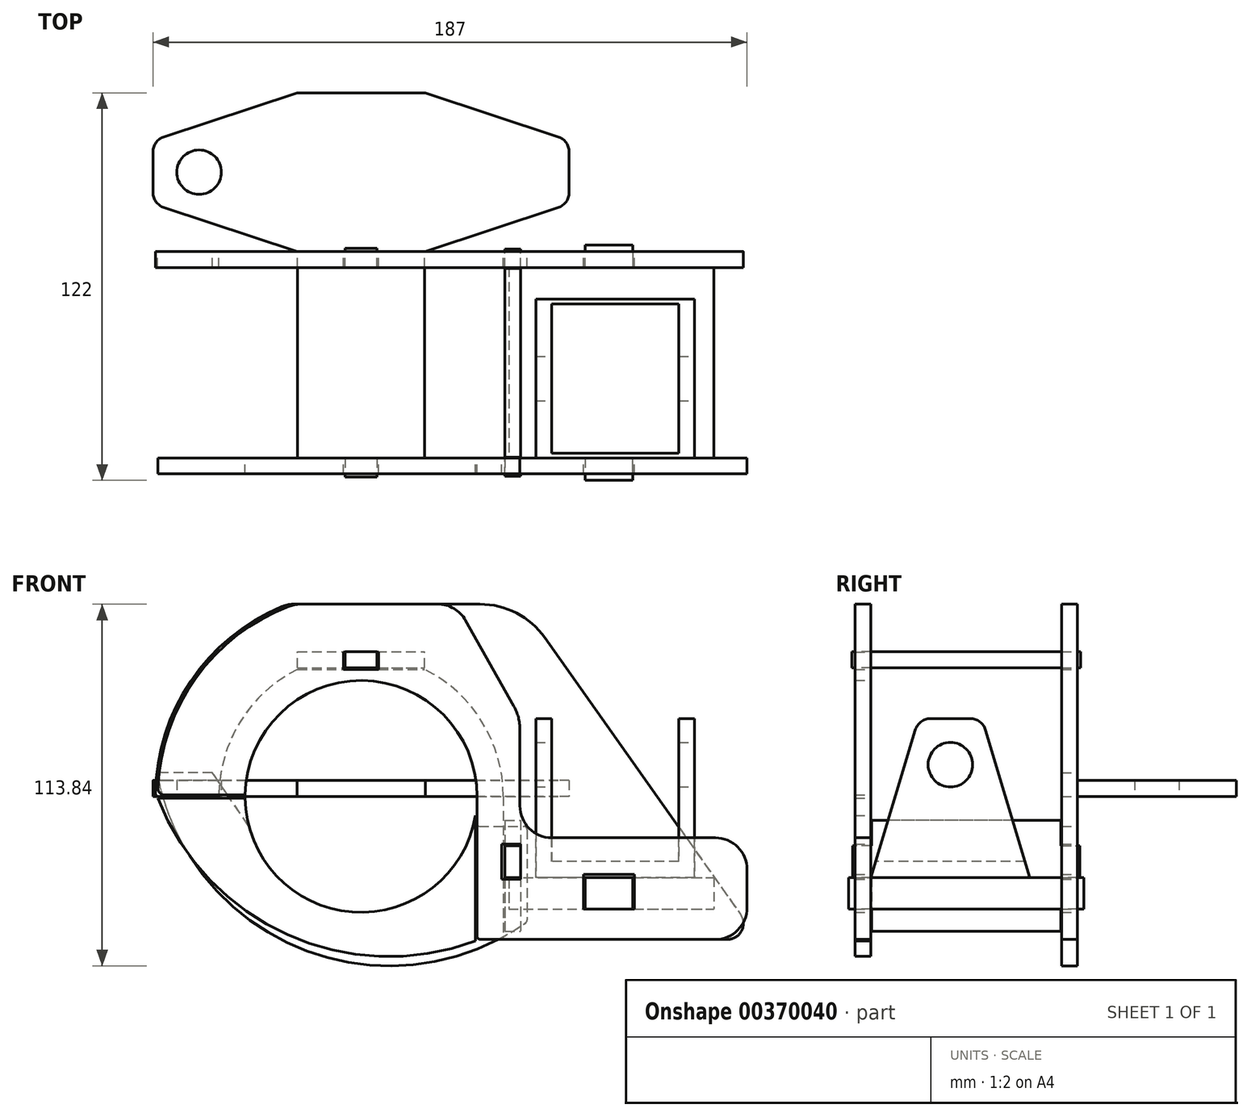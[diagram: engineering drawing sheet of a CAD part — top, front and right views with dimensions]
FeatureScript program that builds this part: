
annotation { "Feature Type Name" : "Feature", "Feature Type Description" : "" }
export const myFeature = defineFeature(function(context is Context, id is Id, definition is map)
    precondition{}
    {
        {
            var Q0;
            Q0=qCreatedBy(makeId("Front.planeOp"),FACE);
            var sketch = newSketch(context, id + "F0", { "sketchPlane" : qUnion([Q0])});
            skArc(sketch, "E0", {"start": v(44.75, 0) * mm, "mid": v(0, 44.75) * mm, "end": v(-44.75, 0) * mm, "construction": true});
            skLineSegment(sketch, "E1", {"start": v(-20, 40.03) * mm, "end": v(-5.5, 40.03) * mm});
            skLineSegment(sketch, "E2", {"start": v(-5.5, 40.03) * mm, "end": v(-5.5, 45.53) * mm});
            skLineSegment(sketch, "E3", {"start": v(-5.5, 45.53) * mm, "end": v(5.5, 45.53) * mm});
            skLineSegment(sketch, "E4", {"start": v(5.5, 45.53) * mm, "end": v(5.5, 40.03) * mm});
            skLineSegment(sketch, "E5", {"start": v(5.5, 40.03) * mm, "end": v(20, 40.03) * mm});
            skPoint(sketch, "E6", {"position": v(0, 45.53) * mm});
            skArc(sketch, "E7", {"start": v(-20, 40.03) * mm, "mid": v(-38.06, 23.53) * mm, "end": v(-44.75, 0) * mm});
            skArc(sketch, "E8", {"start": v(44.75, 0) * mm, "mid": v(38.06, 23.53) * mm, "end": v(20, 40.03) * mm});
            skArc(sketch, "E9.0", {"start": v(-24.92, 59.76) * mm, "mid": v(-53.6, 36.33) * mm, "end": v(-64.74, 1.02) * mm});
            skLineSegment(sketch, "E10", {"start": v(-63.74, 0) * mm, "end": v(-44.75, 0) * mm});
            skLineSegment(sketch, "E11", {"start": v(-21.07, 60.53) * mm, "end": v(37.4, 60.53) * mm});
            skLineSegment(sketch, "E12", {"start": v(44.75, 0) * mm, "end": v(44.75, -15) * mm});
            skLineSegment(sketch, "E13", {"start": v(44.75, -45) * mm, "end": v(115.34, -45) * mm});
            skArc(sketch, "E14", {"start": v(-36.5, 0) * mm, "mid": v(0, -36.5) * mm, "end": v(36.5, 0) * mm, "construction": true});
            skLineSegment(sketch, "E15", {"start": v(-44.75, 0) * mm, "end": v(-36.5, 0) * mm, "construction": true});
            skLineSegment(sketch, "E16", {"start": v(44.75, 0) * mm, "end": v(36.5, 0) * mm, "construction": true});
            skPoint(sketch, "E17", {"position": v(80, 10) * mm});
            skLineSegment(sketch, "E18", {"start": v(57.82, 49.97) * mm, "end": v(119.42, -37.11) * mm});
            skLineSegment(sketch, "E19.bottom", {"start": v(70, -24.5) * mm, "end": v(86, -24.5) * mm});
            skLineSegment(sketch, "E19.top", {"start": v(70, -35.5) * mm, "end": v(86, -35.5) * mm});
            skLineSegment(sketch, "E19.left", {"start": v(70, -24.5) * mm, "end": v(70, -35.5) * mm});
            skLineSegment(sketch, "E19.right", {"start": v(86, -24.5) * mm, "end": v(86, -35.5) * mm});
            skPoint(sketch, "E20.visualSharp", {"position": v(-22.99, 60.53) * mm});
            skArc(sketch, "E20.filletArc", {"start": v(-21.07, 60.53) * mm, "mid": v(-23.04, 60.34) * mm, "end": v(-24.92, 59.76) * mm});
            skPoint(sketch, "E21.visualSharp", {"position": v(50.35, 60.53) * mm});
            skArc(sketch, "E21.filletArc", {"start": v(57.82, 49.97) * mm, "mid": v(48.9, 57.73) * mm, "end": v(37.4, 60.53) * mm});
            skPoint(sketch, "E22.visualSharp", {"position": v(125, -45) * mm});
            skArc(sketch, "E22.filletArc", {"start": v(115.34, -45) * mm, "mid": v(119.78, -42.3) * mm, "end": v(119.42, -37.11) * mm});
            skLineSegment(sketch, "E23", {"start": v(44.75, -15) * mm, "end": v(50.25, -15) * mm});
            skLineSegment(sketch, "E24", {"start": v(50.25, -15) * mm, "end": v(50.25, -26) * mm});
            skLineSegment(sketch, "E25", {"start": v(50.25, -26) * mm, "end": v(44.75, -26) * mm});
            skLineSegment(sketch, "E26.trimOffspring", {"start": v(44.75, -26) * mm, "end": v(44.75, -45) * mm});
            skPoint(sketch, "E27.visualSharp", {"position": v(-64.75, 0) * mm});
            skArc(sketch, "E27.filletArc", {"start": v(-64.74, 1.02) * mm, "mid": v(-64.45, 0.3) * mm, "end": v(-63.74, 0) * mm});
            skSolve(sketch);
        }
        {
            var Q0;
            Q0=qSketchRegion(id+"F0",true);
            var Q1;
            Q1=qConstructionFilter(qBodyType(qCreatedBy(id+"F0",EDGE),BodyType.WIRE),ConstructionObject.NO);
            extrude(context, id + "F1", {"entities" : qUnion([Q0]), "surfaceEntities" : qUnion([Q1]), "depth" : 5 * mm});
        }
        {
            var Q0;
            Q0=qCreatedBy(makeId("Front.planeOp"),FACE);
            var sketch = newSketch(context, id + "F2", { "sketchPlane" : qUnion([Q0])});
            skArc(sketch, "E28", {"start": v(-35.15, -9.84) * mm, "mid": v(-0.7, -36.5) * mm, "end": v(34.75, -11.18) * mm});
            skLineSegment(sketch, "E29", {"start": v(-35.26, -9.45) * mm, "end": v(0, 0) * mm, "construction": true});
            skLineSegment(sketch, "E30", {"start": v(35.26, -9.45) * mm, "end": v(0, 0) * mm, "construction": true});
            skLineSegment(sketch, "E31", {"start": v(-35.5, -9.1) * mm, "end": v(-46.81, 7.5) * mm});
            skLineSegment(sketch, "E32", {"start": v(-46.81, 7.5) * mm, "end": v(-63.1, 7.5) * mm});
            skLineSegment(sketch, "E33", {"start": v(37.13, -9.45) * mm, "end": v(51.25, -9.45) * mm});
            skLineSegment(sketch, "E34", {"start": v(52.25, -10.45) * mm, "end": v(52.25, -38.93) * mm});
            skArc(sketch, "E35", {"start": v(-64.08, 6.3) * mm, "mid": v(-18.57, -48.04) * mm, "end": v(51.83, -39.75) * mm});
            skPoint(sketch, "E36.visualSharp", {"position": v(-35.26, -9.45) * mm});
            skArc(sketch, "E36.filletArc", {"start": v(-35.15, -9.84) * mm, "mid": v(-35.3, -9.46) * mm, "end": v(-35.5, -9.1) * mm});
            skPoint(sketch, "E37.visualSharp", {"position": v(35.26, -9.45) * mm});
            skArc(sketch, "E37.filletArc", {"start": v(37.13, -9.45) * mm, "mid": v(35.65, -9.93) * mm, "end": v(34.75, -11.18) * mm});
            skPoint(sketch, "E38.visualSharp", {"position": v(-64.31, 7.5) * mm});
            skArc(sketch, "E38.filletArc", {"start": v(-63.1, 7.5) * mm, "mid": v(-63.87, 7.13) * mm, "end": v(-64.08, 6.3) * mm});
            skPoint(sketch, "E39.visualSharp", {"position": v(52.25, -39.45) * mm});
            skArc(sketch, "E39.filletArc", {"start": v(51.83, -39.75) * mm, "mid": v(52.14, -39.4) * mm, "end": v(52.25, -38.93) * mm});
            skPoint(sketch, "E40.visualSharp", {"position": v(52.25, -9.45) * mm});
            skArc(sketch, "E40.filletArc", {"start": v(52.25, -10.45) * mm, "mid": v(51.96, -9.74) * mm, "end": v(51.25, -9.45) * mm});
            skSolve(sketch);
        }
        {
            var Q0;
            Q0=qSketchRegion(id+"F2",true);
            extrude(context, id + "F3", {"entities" : qUnion([Q0]), "depth" : 5 * mm});
        }
        {
            var Q0;
            Q0=makeQuery(id+"F1.opExtrude","SWEPT_FACE",FACE,{"disambiguationData":[OSD([sQuery(id+"F0.wireOp",EDGE,"E19.top")])]});
            var sketch = newSketch(context, id + "F4", { "sketchPlane" : qUnion([Q0])});
            skLineSegment(sketch, "E41.bottom", {"start": v(46.5, -5) * mm, "end": v(111, -5) * mm});
            skLineSegment(sketch, "E41.top", {"start": v(46.5, -65) * mm, "end": v(111, -65) * mm});
            skLineSegment(sketch, "E41.left", {"start": v(46.5, -5) * mm, "end": v(46.5, -65) * mm});
            skLineSegment(sketch, "E41.right", {"start": v(111, -5) * mm, "end": v(111, -65) * mm});
            skLineSegment(sketch, "E42", {"start": v(70.5, -5) * mm, "end": v(70.5, 2) * mm});
            skLineSegment(sketch, "E43", {"start": v(70.5, 2) * mm, "end": v(85.5, 2) * mm});
            skLineSegment(sketch, "E44", {"start": v(85.5, 2) * mm, "end": v(85.5, -5) * mm});
            skLineSegment(sketch, "E45", {"start": v(70.5, -65) * mm, "end": v(70.5, -72) * mm});
            skLineSegment(sketch, "E46", {"start": v(70.5, -72) * mm, "end": v(85.5, -72) * mm});
            skLineSegment(sketch, "E47", {"start": v(85.5, -72) * mm, "end": v(85.5, -65) * mm});
            skSolve(sketch);
        }
        {
            var Q0;
            Q0=qSketchRegion(id+"F4",true);
            extrude(context, id + "F5", {"entities" : qUnion([Q0]), "depth" : 10 * mm});
        }
        {
            var Q0;
            {var subQ0=sQuery(id+"F4.wireOp",EDGE,"E41.top");Q0=makeQuery(id+"F5.opExtrude","SWEPT_FACE",FACE,{"disambiguationData":[OSD([subQ0]),TDD([makeQuery(id+"F4.imprint","IMPRINT",EDGE,{"disambiguationData":[TD([[makeQuery(id+"F4.imprint","INTERSECT",VERTEX,{"derivedFrom":[subQ0,sQuery(id+"F4.wireOp",EDGE,"E41.left")]}),-1.0]])],"derivedFrom":subQ0})])]});}
            var sketch = newSketch(context, id + "F6", { "sketchPlane" : qUnion([Q0])});
            skLineSegment(sketch, "E48", {"start": v(60, 24.5) * mm, "end": v(60, -20.5) * mm});
            skLineSegment(sketch, "E49", {"start": v(60, -20.5) * mm, "end": v(100, -20.5) * mm});
            skLineSegment(sketch, "E50", {"start": v(100, -20.5) * mm, "end": v(100, 24.5) * mm});
            skLineSegment(sketch, "E51", {"start": v(100, 24.5) * mm, "end": v(105, 24.5) * mm});
            skLineSegment(sketch, "E52", {"start": v(105, 24.5) * mm, "end": v(105, -25.5) * mm});
            skLineSegment(sketch, "E53", {"start": v(105, -25.5) * mm, "end": v(55, -25.5) * mm});
            skLineSegment(sketch, "E54", {"start": v(55, -25.5) * mm, "end": v(55, 24.5) * mm});
            skLineSegment(sketch, "E55", {"start": v(55, 24.5) * mm, "end": v(60, 24.5) * mm});
            skSolve(sketch);
        }
        {
            var Q0;
            Q0=qSketchRegion(id+"F6",true);
            extrude(context, id + "F7", {"entities" : qUnion([Q0]), "oppositeDirection" : true, "depth" : 50 * mm});
        }
        {
            var Q0;
            Q0=makeQuery(id+"F7.opExtrude","SWEPT_FACE",FACE,{"disambiguationData":[OSD([sQuery(id+"F6.wireOp",EDGE,"E52")])]});
            var sketch = newSketch(context, id + "F8", { "sketchPlane" : qUnion([Q0])});
            skCircle(sketch, "E56", {"center": v(-40, 10) * mm, "radius": 7 * mm});
            skLineSegment(sketch, "E57", {"start": v(-46.28, 24.5) * mm, "end": v(-33.72, 24.5) * mm});
            skPoint(sketch, "E58", {"position": v(-40, 24.5) * mm});
            skLineSegment(sketch, "E59", {"start": v(-65, -25.5) * mm, "end": v(-51.07, 20.94) * mm});
            skLineSegment(sketch, "E60", {"start": v(-28.93, 20.94) * mm, "end": v(-15, -25.5) * mm});
            skPoint(sketch, "E61.visualSharp", {"position": v(-50, 24.5) * mm});
            skArc(sketch, "E61.filletArc", {"start": v(-46.28, 24.5) * mm, "mid": v(-49.26, 23.51) * mm, "end": v(-51.07, 20.94) * mm});
            skPoint(sketch, "E62.visualSharp", {"position": v(-30, 24.5) * mm});
            skArc(sketch, "E62.filletArc", {"start": v(-28.93, 20.94) * mm, "mid": v(-30.74, 23.51) * mm, "end": v(-33.72, 24.5) * mm});
            skLineSegment(sketch, "E63", {"start": v(-46.28, 24.5) * mm, "end": v(-65, 24.5) * mm});
            skLineSegment(sketch, "E64", {"start": v(-65, 24.5) * mm, "end": v(-65, -25.5) * mm});
            skLineSegment(sketch, "E65", {"start": v(-33.72, 24.5) * mm, "end": v(-15, 24.5) * mm});
            skLineSegment(sketch, "E66", {"start": v(-15, 24.5) * mm, "end": v(-15, -25.5) * mm});
            skSolve(sketch);
        }
        {
            var Q0;
            Q0=qSketchRegion(id+"F8",true);
            extrude(context, id + "F9", {"entities" : qUnion([Q0]), "operationType" : NewBodyOperationType.REMOVE, "oppositeDirection" : true, "depth" : 602 * mm});
        }
        {
            var Q0;
            {var subQ0=sQuery(id+"F4.wireOp",EDGE,"E41.top");Q0=makeQuery(id+"F5.opExtrude","SWEPT_FACE",FACE,{"disambiguationData":[OSD([subQ0]),TDD([makeQuery(id+"F4.imprint","IMPRINT",EDGE,{"disambiguationData":[TD([[makeQuery(id+"F4.imprint","INTERSECT",VERTEX,{"derivedFrom":[subQ0,sQuery(id+"F4.wireOp",EDGE,"E41.right")]}),1.0]])],"derivedFrom":subQ0})])]});}
            var sketch = newSketch(context, id + "F10", { "sketchPlane" : qUnion([Q0])});
            skArc(sketch, "E67", {"start": v(36.5, 0) * mm, "mid": v(0.25, 36.5) * mm, "end": v(-36.5, 0.5) * mm});
            skLineSegment(sketch, "E68", {"start": v(-36.5, 0.5) * mm, "end": v(-61.95, 0.5) * mm});
            skArc(sketch, "E69", {"start": v(-22.56, 59.9) * mm, "mid": v(-51.88, 37.47) * mm, "end": v(-63.95, 2.58) * mm});
            skLineSegment(sketch, "E70", {"start": v(-19.04, 60.53) * mm, "end": v(24.15, 60.53) * mm});
            skPoint(sketch, "E71.orphan", {"position": v(0, 64) * mm});
            skLineSegment(sketch, "E72", {"start": v(50, 21.07) * mm, "end": v(50, 0.02) * mm});
            skLineSegment(sketch, "E73", {"start": v(36.5, 0) * mm, "end": v(36.5, -44) * mm});
            skLineSegment(sketch, "E74", {"start": v(37.5, -45) * mm, "end": v(111.5, -45) * mm});
            skLineSegment(sketch, "E75", {"start": v(121.5, -35) * mm, "end": v(121.5, -23) * mm});
            skLineSegment(sketch, "E76", {"start": v(111.5, -13) * mm, "end": v(60, -13) * mm});
            skLineSegment(sketch, "E77", {"start": v(50, -3) * mm, "end": v(50, 0.02) * mm});
            skLineSegment(sketch, "E78.bottom", {"start": v(70, -24.5) * mm, "end": v(86, -24.5) * mm});
            skLineSegment(sketch, "E78.top", {"start": v(70, -35.5) * mm, "end": v(86, -35.5) * mm});
            skLineSegment(sketch, "E78.left", {"start": v(70, -24.5) * mm, "end": v(70, -35.5) * mm});
            skLineSegment(sketch, "E78.right", {"start": v(86, -24.5) * mm, "end": v(86, -35.5) * mm});
            skPoint(sketch, "E79.visualSharp", {"position": v(-20.78, 60.53) * mm});
            skArc(sketch, "E79.filletArc", {"start": v(-19.04, 60.53) * mm, "mid": v(-20.83, 60.37) * mm, "end": v(-22.56, 59.9) * mm});
            skPoint(sketch, "E80.visualSharp", {"position": v(-64, 0.5) * mm});
            skArc(sketch, "E80.filletArc", {"start": v(-63.95, 2.58) * mm, "mid": v(-63.4, 1.11) * mm, "end": v(-61.95, 0.5) * mm});
            skPoint(sketch, "E81.visualSharp", {"position": v(50, 60.53) * mm});
            skPoint(sketch, "E82.visualSharp", {"position": v(50, -13) * mm});
            skArc(sketch, "E82.filletArc", {"start": v(50, -3) * mm, "mid": v(52.93, -10.07) * mm, "end": v(60, -13) * mm});
            skPoint(sketch, "E83.visualSharp", {"position": v(36.5, -45) * mm});
            skArc(sketch, "E83.filletArc", {"start": v(36.5, -44) * mm, "mid": v(36.8, -44.7) * mm, "end": v(37.5, -45) * mm});
            skPoint(sketch, "E84.visualSharp", {"position": v(121.5, -45) * mm});
            skArc(sketch, "E84.filletArc", {"start": v(111.5, -45) * mm, "mid": v(118.57, -42.07) * mm, "end": v(121.5, -35) * mm});
            skPoint(sketch, "E85.visualSharp", {"position": v(121.5, -13) * mm});
            skArc(sketch, "E85.filletArc", {"start": v(121.5, -23) * mm, "mid": v(118.57, -15.93) * mm, "end": v(111.5, -13) * mm});
            skLineSegment(sketch, "E86", {"start": v(32.87, 55.44) * mm, "end": v(48.07, 28.43) * mm});
            skPoint(sketch, "E87.visualSharp", {"position": v(50, 25) * mm});
            skArc(sketch, "E87.filletArc", {"start": v(50, 21.07) * mm, "mid": v(49.5, 24.87) * mm, "end": v(48.07, 28.43) * mm});
            skPoint(sketch, "E88.visualSharp", {"position": v(30, 60.53) * mm});
            skArc(sketch, "E88.filletArc", {"start": v(32.87, 55.44) * mm, "mid": v(29.2, 59.16) * mm, "end": v(24.15, 60.53) * mm});
            skArc(sketch, "E89", {"start": v(-36.5, -0.5) * mm, "mid": v(-2.77, -36.4) * mm, "end": v(36, -6.02) * mm});
            skLineSegment(sketch, "E90", {"start": v(36, -6.02) * mm, "end": v(36, -45.5) * mm});
            skLineSegment(sketch, "E91", {"start": v(-64, -0.5) * mm, "end": v(-36.5, -0.5) * mm});
            skArc(sketch, "E92", {"start": v(-64, -0.5) * mm, "mid": v(-23.22, -43.5) * mm, "end": v(36, -45.5) * mm});
            skLineSegment(sketch, "E93.bottom", {"start": v(-5.5, 40) * mm, "end": v(5.5, 40) * mm});
            skLineSegment(sketch, "E93.top", {"start": v(-5.5, 45.5) * mm, "end": v(5.5, 45.5) * mm});
            skLineSegment(sketch, "E93.left", {"start": v(-5.5, 40) * mm, "end": v(-5.5, 45.5) * mm});
            skLineSegment(sketch, "E93.right", {"start": v(5.5, 40) * mm, "end": v(5.5, 45.5) * mm});
            skPoint(sketch, "E94", {"position": v(0, 40) * mm});
            skLineSegment(sketch, "E95.bottom", {"start": v(44.25, -15) * mm, "end": v(50.25, -15) * mm});
            skLineSegment(sketch, "E95.top", {"start": v(44.25, -26) * mm, "end": v(50.25, -26) * mm});
            skLineSegment(sketch, "E95.left", {"start": v(44.25, -15) * mm, "end": v(44.25, -26) * mm});
            skLineSegment(sketch, "E95.right", {"start": v(50.25, -15) * mm, "end": v(50.25, -26) * mm});
            skSolve(sketch);
        }
        {
            var Q0;
            Q0=qSketchRegion(id+"F10",true);
            extrude(context, id + "F11", {"entities" : qUnion([Q0]), "depth" : 5 * mm});
        }
        {
            var Q0;
            Q0=makeQuery(id+"F1.opExtrude","SWEPT_FACE",FACE,{"disambiguationData":[OSD([sQuery(id+"F0.wireOp",EDGE,"E3")])]});
            var sketch = newSketch(context, id + "F12", { "sketchPlane" : qUnion([Q0])});
            skLineSegment(sketch, "E96.bottom", {"start": v(-20, 5) * mm, "end": v(20, 5) * mm});
            skLineSegment(sketch, "E96.top", {"start": v(-20, 65) * mm, "end": v(20, 65) * mm});
            skLineSegment(sketch, "E96.left", {"start": v(-20, 5) * mm, "end": v(-20, 65) * mm});
            skLineSegment(sketch, "E96.right", {"start": v(20, 5) * mm, "end": v(20, 65) * mm});
            skLineSegment(sketch, "E97.bottom", {"start": v(-5, 5) * mm, "end": v(5, 5) * mm});
            skLineSegment(sketch, "E97.top", {"start": v(-5, -1) * mm, "end": v(5, -1) * mm});
            skLineSegment(sketch, "E97.left", {"start": v(-5, 5) * mm, "end": v(-5, -1) * mm});
            skLineSegment(sketch, "E97.right", {"start": v(5, 5) * mm, "end": v(5, -1) * mm});
            skLineSegment(sketch, "E98.bottom", {"start": v(-5, 65) * mm, "end": v(5, 65) * mm});
            skLineSegment(sketch, "E98.top", {"start": v(-5, 71) * mm, "end": v(5, 71) * mm});
            skLineSegment(sketch, "E98.left", {"start": v(-5, 65) * mm, "end": v(-5, 71) * mm});
            skLineSegment(sketch, "E98.right", {"start": v(5, 65) * mm, "end": v(5, 71) * mm});
            skSolve(sketch);
        }
        {
            var Q0;
            Q0=qSketchRegion(id+"F12",true);
            extrude(context, id + "F13", {"entities" : qUnion([Q0]), "depth" : 5 * mm});
        }
        {
            var Q0;
            Q0=makeQuery(id+"F1.opExtrude","SWEPT_FACE",FACE,{"disambiguationData":[OSD([sQuery(id+"F0.wireOp",EDGE,"E24")])]});
            var sketch = newSketch(context, id + "F14", { "sketchPlane" : qUnion([Q0])});
            skLineSegment(sketch, "E99.bottom", {"start": v(5.25, -7.5) * mm, "end": v(64.75, -7.5) * mm});
            skLineSegment(sketch, "E99.top", {"start": v(5.25, -42.5) * mm, "end": v(64.75, -42.5) * mm});
            skLineSegment(sketch, "E99.left", {"start": v(5.25, -7.5) * mm, "end": v(5.25, -42.5) * mm});
            skLineSegment(sketch, "E99.right", {"start": v(64.75, -7.5) * mm, "end": v(64.75, -42.5) * mm});
            skLineSegment(sketch, "E100.bottom", {"start": v(5.25, -15.5) * mm, "end": v(-0.75, -15.5) * mm});
            skLineSegment(sketch, "E100.top", {"start": v(5.25, -25.5) * mm, "end": v(-0.75, -25.5) * mm});
            skLineSegment(sketch, "E100.left", {"start": v(5.25, -15.5) * mm, "end": v(5.25, -25.5) * mm});
            skLineSegment(sketch, "E100.right", {"start": v(-0.75, -15.5) * mm, "end": v(-0.75, -25.5) * mm});
            skLineSegment(sketch, "E101.bottom", {"start": v(64.75, -15.5) * mm, "end": v(70.75, -15.5) * mm});
            skLineSegment(sketch, "E101.left", {"start": v(64.75, -15.5) * mm, "end": v(64.75, -26) * mm});
            skLineSegment(sketch, "E101.right", {"start": v(70.75, -15.5) * mm, "end": v(70.75, -25.5) * mm});
            skLineSegment(sketch, "E102", {"start": v(70.75, -25.5) * mm, "end": v(64.75, -25.5) * mm});
            skSolve(sketch);
        }
        {
            var Q0;
            Q0=qSketchRegion(id+"F14",true);
            extrude(context, id + "F15", {"entities" : qUnion([Q0]), "depth" : 5 * mm});
        }
        {
            var Q0;
            Q0=qCreatedBy(makeId("Top.planeOp"),FACE);
            var sketch = newSketch(context, id + "F16", { "sketchPlane" : qUnion([Q0])});
            skLineSegment(sketch, "E103.bottom", {"start": v(-20.2, 0) * mm, "end": v(20.2, 0) * mm});
            skLineSegment(sketch, "E103.top", {"start": v(-20.2, 50) * mm, "end": v(20.2, 50) * mm});
            skLineSegment(sketch, "E103.left", {"start": v(-20.2, 0) * mm, "end": v(-20.2, 50) * mm});
            skLineSegment(sketch, "E103.right", {"start": v(20.2, 0) * mm, "end": v(20.2, 50) * mm});
            skCircle(sketch, "E104", {"center": v(-51, 25) * mm, "radius": 7 * mm});
            skLineSegment(sketch, "E105", {"start": v(-20.2, 0) * mm, "end": v(-62.07, 13.86) * mm});
            skLineSegment(sketch, "E106", {"start": v(-65.5, 18.61) * mm, "end": v(-65.5, 31.39) * mm});
            skLineSegment(sketch, "E107", {"start": v(-62.07, 36.14) * mm, "end": v(-20.2, 50) * mm});
            skLineSegment(sketch, "E108", {"start": v(20.2, 0) * mm, "end": v(62.07, 13.86) * mm});
            skLineSegment(sketch, "E109", {"start": v(65.5, 18.61) * mm, "end": v(65.5, 31.39) * mm});
            skLineSegment(sketch, "E110", {"start": v(62.07, 36.14) * mm, "end": v(20.2, 50) * mm});
            skPoint(sketch, "E111", {"position": v(-65.5, 25) * mm});
            skPoint(sketch, "E112", {"position": v(65.5, 25) * mm});
            skPoint(sketch, "E113.visualSharp", {"position": v(-65.5, 15) * mm});
            skArc(sketch, "E113.filletArc", {"start": v(-65.5, 18.61) * mm, "mid": v(-64.55, 15.68) * mm, "end": v(-62.07, 13.86) * mm});
            skPoint(sketch, "E114.visualSharp", {"position": v(-65.5, 35) * mm});
            skArc(sketch, "E114.filletArc", {"start": v(-62.07, 36.14) * mm, "mid": v(-64.55, 34.32) * mm, "end": v(-65.5, 31.39) * mm});
            skPoint(sketch, "E115.visualSharp", {"position": v(65.5, 35) * mm});
            skArc(sketch, "E115.filletArc", {"start": v(65.5, 31.39) * mm, "mid": v(64.55, 34.32) * mm, "end": v(62.07, 36.14) * mm});
            skPoint(sketch, "E116.visualSharp", {"position": v(65.5, 15) * mm});
            skArc(sketch, "E116.filletArc", {"start": v(62.07, 13.86) * mm, "mid": v(64.55, 15.68) * mm, "end": v(65.5, 18.61) * mm});
            skSolve(sketch);
        }
        {
            var Q0;
            Q0=qSketchRegion(id+"F16",true);
            extrude(context, id + "F17", {"entities" : qUnion([Q0]), "depth" : 5 * mm});
        }
    });
